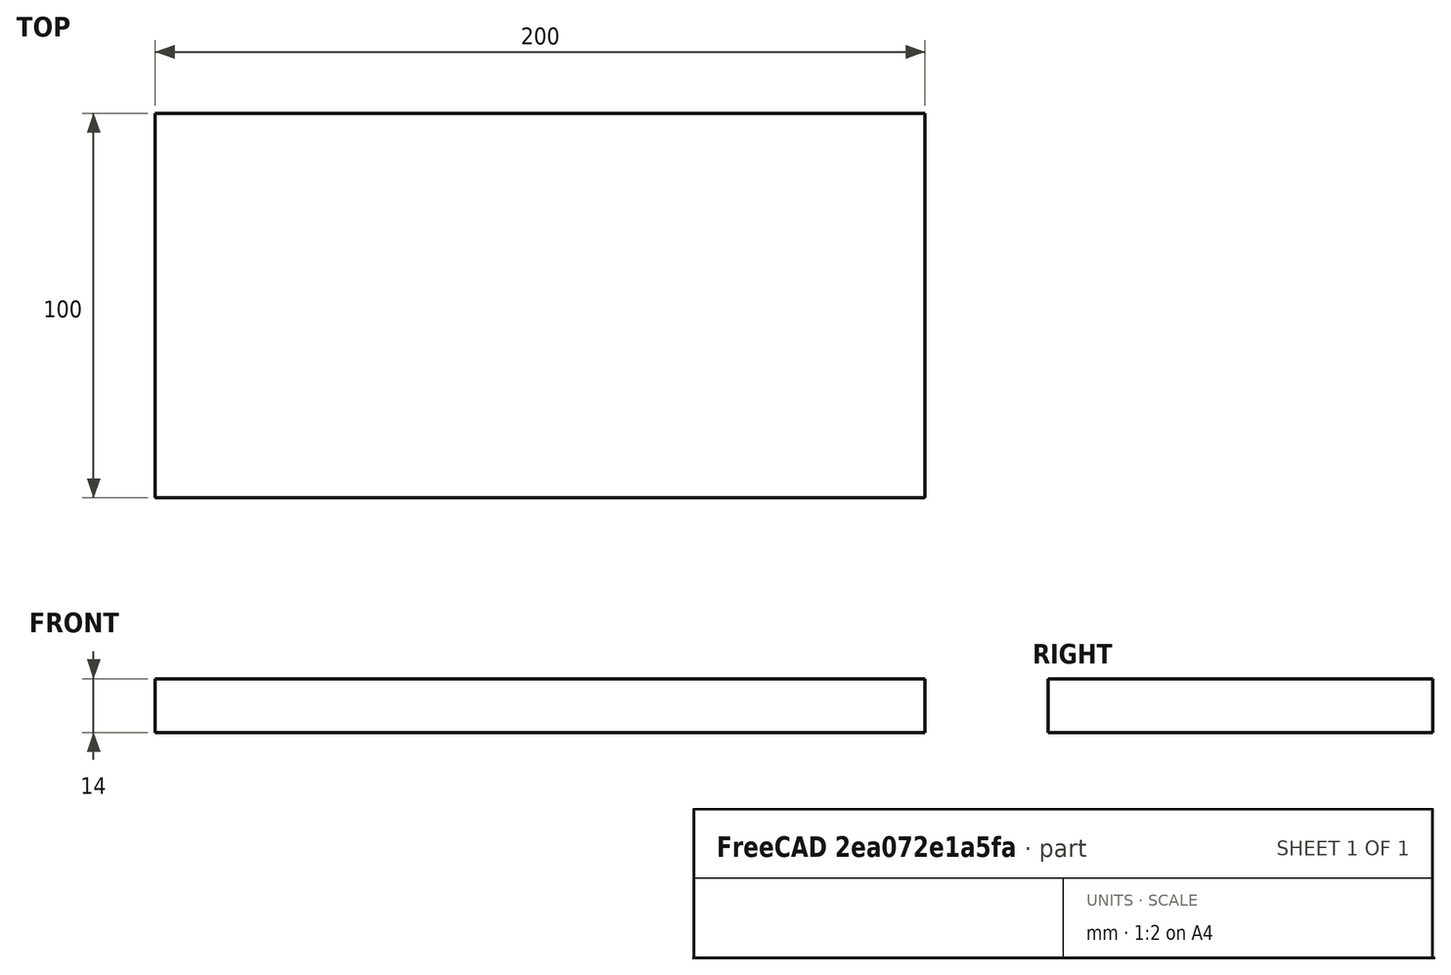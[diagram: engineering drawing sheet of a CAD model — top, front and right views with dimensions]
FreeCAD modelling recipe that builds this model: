
FCSTD DOCUMENT  (FreeCAD 0.19R24276 (Git))
Label: Plate_200x100
License: All rights reserved
LicenseURL: http://en.wikipedia.org/wiki/All_rights_reserved
objects: Sketcher::SketchObject×1, PartDesign::Pad×1, PartDesign::Body×1
note: 4 computed .brp shape members not serialized (recipe doc carries the construction recipe); baked Part::Feature solids carry a one-line shape summary decoded from their .brp

FEATURE [Sketcher::SketchObject] Sketch
  FullyConstrained = true
  MapMode = 5
  Support = -> [XY_Plane]
  sketch-geometry (4):
    g0: LineSegment StartX=0 StartY=0 StartZ=0 EndX=200 EndY=0 EndZ=0
    g1: LineSegment StartX=200 StartY=0 StartZ=0 EndX=200 EndY=100 EndZ=0
    g2: LineSegment StartX=200 StartY=100 StartZ=0 EndX=0 EndY=100 EndZ=0
    g3: LineSegment StartX=0 StartY=100 StartZ=0 EndX=0 EndY=0 EndZ=0
  constraints (11):
    c: Coincident(g0,g1)
    c: Coincident(g1,g2)
    c: Coincident(g2,g3)
    c: Coincident(g3,g0)
    c: Horizontal(g0)
    c: Horizontal(g2)
    c: Vertical(g1)
    c: Vertical(g3)
    c: Coincident(g0,g-1)
    c: DistanceY(g1,g1) = 100
    c: DistanceX(g0,g0) = 200
FEATURE [PartDesign::Pad] Pad
  Direction = (1,1,1)
  Length = 14
  Length2 = 100
  Profile = -> Sketch
  Type = 0
FEATURE [PartDesign::Body] Body
  Group = -> [Sketch,Pad]
  Origin = -> Origin
  Tip = -> Pad
